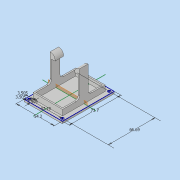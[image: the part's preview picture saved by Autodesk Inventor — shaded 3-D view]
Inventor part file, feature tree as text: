
AUTODESK INVENTOR PART (.ipt)
format: ipt  version: 2017 (Build 210142000, 142)  size: 141,824 bytes
history: native  units: in
note: dims shown in document units (in); Inventor stores cm internally (conversion verified against a paired STEP export)
features: extrude x4, sketch x3, plane x1, fillet x1
ambient origin geometry x8: Origin, YZ Plane, XZ Plane, XY Plane, X Axis, Y Axis, Z Axis, Center Point
bodies: Solid1 (feature_tree)
feature tree (9):
  sketch  "Sketch1"  dims[d0=2.1339in d1=2.9016in]
  extrude  "baseplate"  Depth=2.9016in
  extrude  "perimeter"  Depth=1.4961in
  plane  "Work Plane1"
  extrude  "holders"  Depth=0.0787in
  extrude  "Extrusion4"  Depth=0.315in TaperAngle=0.0deg
  fillet  "Fillet1"  Radius=0.1969in
  sketch  "Sketch2"  dims[d2=0.125in d3=0.0in d4=1.4961in]
  sketch  "Sketch3"  dims[d5=2.2244in d6=0.0787in d7=0.315in d8=0.0in d10=0.1969in d11=0.0787in d12=1.1811in d13=1.4961in d14=0.4724in d15=0.0in d16=0.138in d17=0.138in d18=0.138in d19=0.7874in d21=1.8579in d22=0.7874in d24=2.6256in d27=0.3937in d28=0.0in d29=0.1969in]
